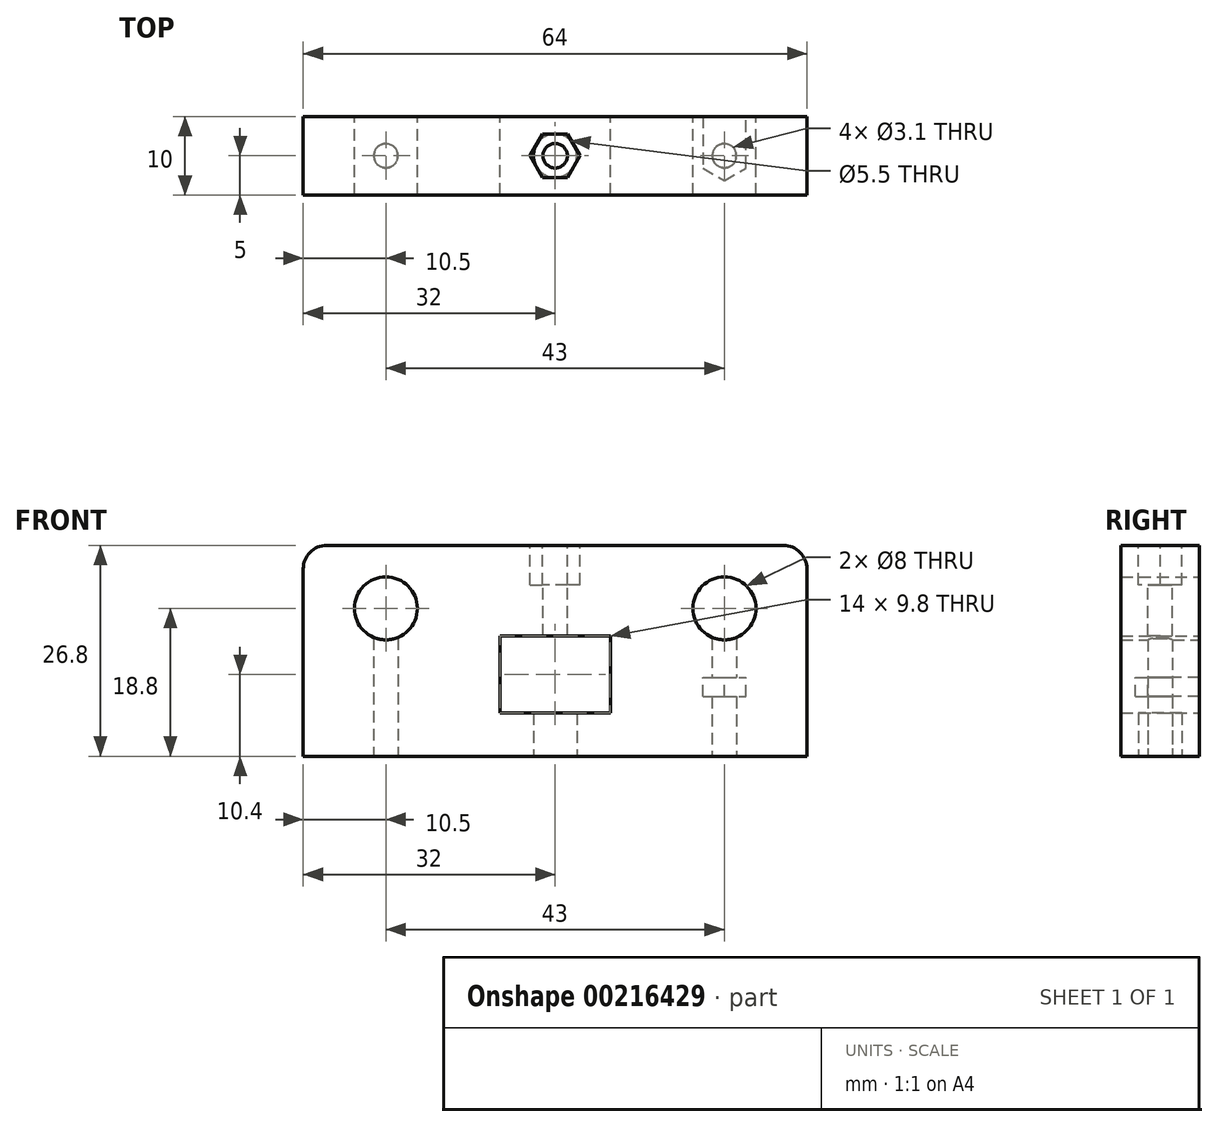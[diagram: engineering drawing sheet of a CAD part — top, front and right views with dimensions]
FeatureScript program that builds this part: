
annotation { "Feature Type Name" : "Feature", "Feature Type Description" : "" }
export const myFeature = defineFeature(function(context is Context, id is Id, definition is map)
    precondition{}
    {
        {
            var Q0;
            Q0=qCreatedBy(makeId("Front.planeOp"),FACE);
            var sketch = newSketch(context, id + "F0", { "sketchPlane" : qUnion([Q0])});
            skLineSegment(sketch, "E0.bottom", {"start": v(32, 14) * mm, "end": v(-32, 14) * mm});
            skLineSegment(sketch, "E0.top", {"start": v(32, -14) * mm, "end": v(-32, -14) * mm});
            skLineSegment(sketch, "E0.left", {"start": v(32, 14) * mm, "end": v(32, -14) * mm});
            skLineSegment(sketch, "E0.right", {"start": v(-32, 14) * mm, "end": v(-32, -14) * mm});
            skPoint(sketch, "E0.middle", {"position": v(0, 0) * mm});
            skLineSegment(sketch, "E1", {"start": v(-32, 6) * mm, "end": v(32, 6) * mm, "construction": true});
            skLineSegment(sketch, "E2", {"start": v(0, 14) * mm, "end": v(0, -14) * mm, "construction": true});
            skCircle(sketch, "E3", {"center": v(-21.5, 6) * mm, "radius": 4 * mm});
            skCircle(sketch, "E4", {"center": v(21.5, 6) * mm, "radius": 4 * mm});
            skLineSegment(sketch, "E5.bottom", {"start": v(7, 2.5) * mm, "end": v(-7, 2.5) * mm});
            skLineSegment(sketch, "E5.top", {"start": v(7, -7.3) * mm, "end": v(-7, -7.3) * mm});
            skLineSegment(sketch, "E5.left", {"start": v(7, 2.5) * mm, "end": v(7, -7.3) * mm});
            skLineSegment(sketch, "E5.right", {"start": v(-7, 2.5) * mm, "end": v(-7, -7.3) * mm});
            skPoint(sketch, "E5.middle", {"position": v(0, -2.4) * mm});
            skPoint(sketch, "E6.orphan", {"position": v(-32, -14) * mm});
            skPoint(sketch, "E7.orphan", {"position": v(32, -14) * mm});
            skSolve(sketch);
        }
        {
            var Q0;
            Q0 = qSketchRegion(id + "F0", true);
            extrude(context, id + "F1", {"entities" : qUnion([Q0]), "endBound" : BoundingType.SYMMETRIC, "depth" : 10 * mm});
        }
        {
            var Q0;
            Q0=makeQuery(id+"F1.opExtrude","SWEPT_FACE",FACE,{"disambiguationData":[OSD([sQuery(id+"F0.wireOp",EDGE,"E0.top")])]});
            cPlane(context, id + "F2", {"entities" : qUnion([Q0]), "cplaneType" : CPlaneType.OFFSET, "offset" : 10 * mm, "oppositeDirection" : true, "width" : 150 * mm, "height" : 150 * mm});
        }
        {
            var Q0;
            Q0=qCreatedBy(id+"F2.planeOp",FACE);
            var sketch = newSketch(context, id + "F3", { "sketchPlane" : qUnion([Q0])});
            skCircle(sketch, "E8.cCircle", {"center": v(21.5, 0) * mm, "radius": 2.75 * mm, "construction": true});
            skLineSegment(sketch, "E8.0", {"start": v(18.75, -1.59) * mm, "end": v(18.75, 1.59) * mm});
            skLineSegment(sketch, "E8.1", {"start": v(18.75, 1.59) * mm, "end": v(21.5, 3.18) * mm});
            skLineSegment(sketch, "E8.2", {"start": v(21.5, 3.18) * mm, "end": v(24.25, 1.59) * mm});
            skLineSegment(sketch, "E8.3", {"start": v(24.25, 1.59) * mm, "end": v(24.25, -5) * mm});
            skPoint(sketch, "E8.0.midPoint", {"position": v(18.75, 0) * mm});
            skLineSegment(sketch, "E9", {"start": v(18.75, -1.59) * mm, "end": v(18.75, -5) * mm});
            skLineSegment(sketch, "E10", {"start": v(18.75, -5) * mm, "end": v(24.25, -5) * mm});
            skSolve(sketch);
        }
        {
            var Q0;
            Q0 = qSketchRegion(id + "F3", true);
            var Q1;
            Q1=makeQuery(id+"F1.opExtrude","SWEPT_FACE",FACE,{"disambiguationData":[OSD([sQuery(id+"F0.wireOp",EDGE,"E0.top")])]});
            extrude(context, id + "F4", {"entities" : qUnion([Q0, Q1]), "operationType" : NewBodyOperationType.REMOVE, "endBound" : BoundingType.SYMMETRIC, "depth" : 2.4 * mm});
        }
        {
            var Q0;
            Q0 = qSketchRegion(id + "F3", true);
            extrude(context, id + "F5", {"entities" : qUnion([Q0]), "operationType" : NewBodyOperationType.REMOVE, "endBound" : BoundingType.SYMMETRIC, "depth" : 2.4 * mm});
        }
        {
            var Q0;
            Q0=makeQuery(id+"F4.boolean.opBoolean","COPY",FACE,{"derivedFrom":makeQuery(id+"F4.opExtrude","CAP_FACE",FACE,{"disambiguationData":[OSD([sQuery(id+"F0.wireOp",EDGE,"E0.top")])],"isStart":true})});
            var sketch = newSketch(context, id + "F6", { "sketchPlane" : qUnion([Q0])});
            skPoint(sketch, "E11", {"position": v(21.5, 0) * mm});
            skPoint(sketch, "E12", {"position": v(-21.5, 0) * mm});
            skSolve(sketch);
        }
        {
            var Q0;
            Q0=sQuery(id+"F6.wireOp",VERTEX,"E11");
            var Q1;
            Q1=sQuery(id+"F6.wireOp",VERTEX,"E12");
            var Q2;
            Q2=makeQuery(id+"F1.opExtrude","SWEPT_BODY",BODY,{"disambiguationData":[OSD([sQuery(id+"F0.wireOp",EDGE,"E0.bottom"),sQuery(id+"F0.wireOp",EDGE,"E0.top"),sQuery(id+"F0.wireOp",EDGE,"E0.left"),sQuery(id+"F0.wireOp",EDGE,"E0.right"),sQuery(id+"F0.wireOp",EDGE,"E3"),sQuery(id+"F0.wireOp",EDGE,"E4"),sQuery(id+"F0.wireOp",EDGE,"E5.bottom"),sQuery(id+"F0.wireOp",EDGE,"E5.top"),sQuery(id+"F0.wireOp",EDGE,"E5.left"),sQuery(id+"F0.wireOp",EDGE,"E5.right")])]});
            hole(context, id + "F7", {"style" : HoleStyle.SIMPLE, "endStyle" : HoleEndStyle.BLIND, "holeDiameter" : 3.1 * mm, "holeDepth" : 15 * mm, "locations" : qUnion([Q0, Q1]), "scope" : qUnion([Q2])});
        }
        {
            var Q0;
            Q0=makeQuery(id+"F4.boolean.opBoolean","COPY",FACE,{"derivedFrom":makeQuery(id+"F4.opExtrude","CAP_FACE",FACE,{"disambiguationData":[OSD([sQuery(id+"F0.wireOp",EDGE,"E0.top")])],"isStart":true})});
            var sketch = newSketch(context, id + "F8", { "sketchPlane" : qUnion([Q0])});
            skCircle(sketch, "E13", {"center": v(0, 0) * mm, "radius": 2.75 * mm});
            skSolve(sketch);
        }
        {
            var Q0;
            Q0 = qSketchRegion(id + "F8", true);
            extrude(context, id + "F9", {"entities" : qUnion([Q0]), "operationType" : NewBodyOperationType.REMOVE, "endBound" : BoundingType.UP_TO_NEXT, "oppositeDirection" : true, "depth" : 25 * mm});
        }
        {
            var Q0;
            Q0=makeQuery(id+"F1.opExtrude","SWEPT_FACE",FACE,{"disambiguationData":[OSD([sQuery(id+"F0.wireOp",EDGE,"E0.bottom")])]});
            var sketch = newSketch(context, id + "F10", { "sketchPlane" : qUnion([Q0])});
            skCircle(sketch, "E14.cCircle", {"center": v(0, 0) * mm, "radius": 2.75 * mm, "construction": true});
            skLineSegment(sketch, "E14.0", {"start": v(1.59, -2.75) * mm, "end": v(-1.59, -2.75) * mm});
            skLineSegment(sketch, "E14.1", {"start": v(-1.59, -2.75) * mm, "end": v(-3.18, 0) * mm});
            skLineSegment(sketch, "E14.2", {"start": v(-3.18, 0) * mm, "end": v(-1.59, 2.75) * mm});
            skLineSegment(sketch, "E14.3", {"start": v(-1.59, 2.75) * mm, "end": v(1.59, 2.75) * mm});
            skLineSegment(sketch, "E14.4", {"start": v(1.59, 2.75) * mm, "end": v(3.18, 0) * mm});
            skLineSegment(sketch, "E14.5", {"start": v(3.18, 0) * mm, "end": v(1.59, -2.75) * mm});
            skPoint(sketch, "E14.0.midPoint", {"position": v(0, -2.75) * mm});
            skCircle(sketch, "E15", {"center": v(0, 0) * mm, "radius": 1.55 * mm});
            skSolve(sketch);
        }
        {
            var Q0;
            Q0 = qSketchRegion(id + "F10", true);
            extrude(context, id + "F11", {"entities" : qUnion([Q0]), "operationType" : NewBodyOperationType.REMOVE, "oppositeDirection" : true, "depth" : 5 * mm});
        }
        {
            var Q0;
            Q0=makeQuery(id+"F11.boolean.opBoolean","SPLIT",FACE,{"disambiguationData":[TD([makeQuery(id+"F11.opExtrude","SWEPT_FACE",FACE,{"disambiguationData":[OSD([sQuery(id+"F10.wireOp",EDGE,"E15")])]})])],"derivedFrom":makeQuery(id+"F1.opExtrude","SWEPT_FACE",FACE,{"disambiguationData":[OSD([sQuery(id+"F0.wireOp",EDGE,"E0.bottom")])]})});
            extrude(context, id + "F12", {"entities" : qUnion([Q0]), "operationType" : NewBodyOperationType.REMOVE, "endBound" : BoundingType.UP_TO_NEXT, "oppositeDirection" : true, "depth" : 25 * mm});
        }
        {
            var Q0;
            Q0=makeQuery(id+"F1.opExtrude","SWEPT_EDGE",EDGE,{"disambiguationData":[OSD([sQuery(id+"F0.wireOp",EDGE,"E0.bottom"),sQuery(id+"F0.wireOp",EDGE,"E0.left")])]});
            var Q1;
            Q1=makeQuery(id+"F1.opExtrude","SWEPT_EDGE",EDGE,{"disambiguationData":[OSD([sQuery(id+"F0.wireOp",EDGE,"E0.bottom"),sQuery(id+"F0.wireOp",EDGE,"E0.right")])]});
            var Q2;
            Q2=makeQuery(id+"F4.boolean.opBoolean","COPY",EDGE,{"derivedFrom":makeQuery(id+"F4.opExtrude","CAP_EDGE",EDGE,{"disambiguationData":[OSD([sQuery(id+"F0.wireOp",EDGE,"E0.top"),sQuery(id+"F0.wireOp",EDGE,"E0.left")])],"isStart":true})});
            var Q3;
            Q3=makeQuery(id+"F4.boolean.opBoolean","COPY",EDGE,{"derivedFrom":makeQuery(id+"F4.opExtrude","CAP_EDGE",EDGE,{"disambiguationData":[OSD([sQuery(id+"F0.wireOp",EDGE,"E0.top"),sQuery(id+"F0.wireOp",EDGE,"E0.right")])],"isStart":true})});
            fillet(context, id + "F13", {"entities" : qUnion([Q0, Q1, Q2, Q3]), "radius" : 3 * mm, "tangentPropagation" : true, "allowEdgeOverflow" : false});
        }
    });
